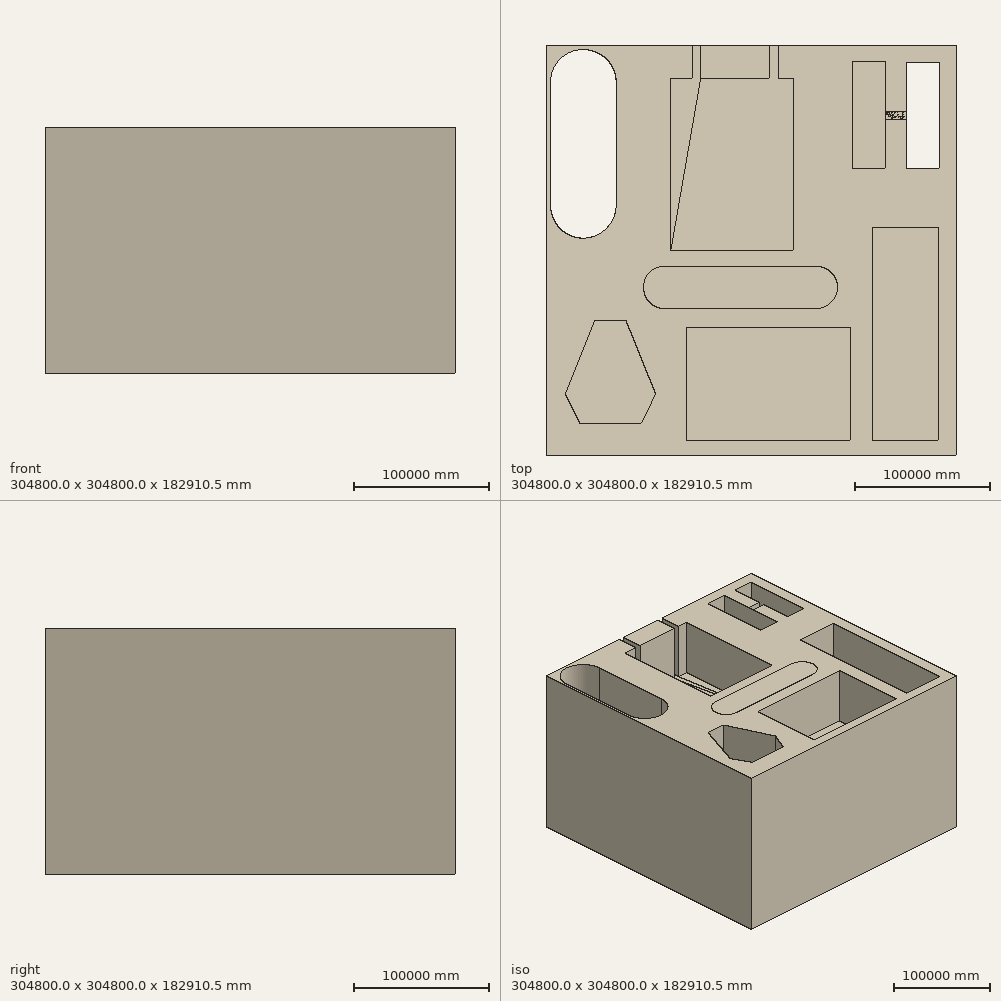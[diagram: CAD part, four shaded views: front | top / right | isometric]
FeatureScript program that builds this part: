
annotation { "Feature Type Name" : "Feature", "Feature Type Description" : "" }
export const myFeature = defineFeature(function(context is Context, id is Id, definition is map)
    precondition{}
    {
        {
            var Q0;
            Q0=qCreatedBy(makeId("Top.planeOp"),FACE);
            var sketch = newSketch(context, id + "F0", { "sketchPlane" : qUnion([Q0])});
            skLineSegment(sketch, "E0.bottom", {"start": v(152400, 152400) * mm, "end": v(-152400, 152400) * mm});
            skLineSegment(sketch, "E0.top", {"start": v(152400, -152400) * mm, "end": v(-152400, -152400) * mm});
            skLineSegment(sketch, "E0.left", {"start": v(152400, 152400) * mm, "end": v(152400, -152400) * mm});
            skLineSegment(sketch, "E0.right", {"start": v(-152400, 152400) * mm, "end": v(-152400, -152400) * mm});
            skPoint(sketch, "E0.middle", {"position": v(0, 0) * mm});
            skLineSegment(sketch, "E1", {"start": v(-149352, 152400) * mm, "end": v(-149352, 124968) * mm});
            skLineSegment(sketch, "E2", {"start": v(-149352, 124968) * mm, "end": v(-152400, 124968) * mm});
            skLineSegment(sketch, "E3.bottom", {"start": v(-149352, 124968) * mm, "end": v(-100584, 124968) * mm});
            skLineSegment(sketch, "E3.top", {"start": v(-149352, 33528) * mm, "end": v(-100584, 33528) * mm});
            skLineSegment(sketch, "E3.left", {"start": v(-149352, 124968) * mm, "end": v(-149352, 33528) * mm});
            skLineSegment(sketch, "E3.right", {"start": v(-100584, 124968) * mm, "end": v(-100584, 33528) * mm});
            skArc(sketch, "E4", {"start": v(-100584, 124968) * mm, "mid": v(-124968, 149352) * mm, "end": v(-149352, 124968) * mm});
            skArc(sketch, "E5", {"start": v(-100584, 33528) * mm, "mid": v(-124968, 9144) * mm, "end": v(-149352, 33528) * mm});
            skLineSegment(sketch, "E6", {"start": v(-124968, 124968) * mm, "end": v(-124968, 149352) * mm});
            skLineSegment(sketch, "E7.bottom", {"start": v(139614.91, 140126.75) * mm, "end": v(115230.91, 140126.75) * mm});
            skLineSegment(sketch, "E7.top", {"start": v(139614.91, 60878.75) * mm, "end": v(115230.91, 60878.75) * mm});
            skLineSegment(sketch, "E7.left", {"start": v(139614.91, 140126.75) * mm, "end": v(139614.91, 60878.75) * mm});
            skLineSegment(sketch, "E7.right", {"start": v(115230.91, 140126.75) * mm, "end": v(115230.91, 60878.75) * mm});
            skSolve(sketch);
        }
        {
            var Q0;
            {var subQ7=sQuery(id+"F0.wireOp",EDGE,"E0.top");Q0=makeQuery(id+"F0.imprint","IMPRINT",FACE,{"disambiguationData":[TD([[makeQuery(id+"F0.imprint","IMPRINT",EDGE,{"derivedFrom":subQ7}),-1.0]])]});}
            var sketch = newSketch(context, id + "F1", { "sketchPlane" : qUnion([Q0])});
            skLineSegment(sketch, "E8.bottom", {"start": v(115322.87, 103222.92) * mm, "end": v(99778.07, 103222.92) * mm});
            skLineSegment(sketch, "E8.top", {"start": v(115322.87, 97126.92) * mm, "end": v(99778.07, 97126.92) * mm});
            skLineSegment(sketch, "E8.left", {"start": v(115322.87, 103222.92) * mm, "end": v(115322.87, 97126.92) * mm});
            skLineSegment(sketch, "E8.right", {"start": v(99778.07, 103222.92) * mm, "end": v(99778.07, 97126.92) * mm});
            skSolve(sketch);
        }
        {
            var Q0;
            {var subQ7=sQuery(id+"F0.wireOp",EDGE,"E0.top");Q0=makeQuery(id+"F0.imprint","IMPRINT",FACE,{"disambiguationData":[TD([[makeQuery(id+"F0.imprint","IMPRINT",EDGE,{"derivedFrom":subQ7}),-1.0]])]});}
            var sketch = newSketch(context, id + "F2", { "sketchPlane" : qUnion([Q0])});
            skLineSegment(sketch, "E9.bottom", {"start": v(99736.5, 140255.87) * mm, "end": v(75352.5, 140255.87) * mm});
            skLineSegment(sketch, "E9.top", {"start": v(99736.5, 61007.87) * mm, "end": v(75352.5, 61007.87) * mm});
            skLineSegment(sketch, "E9.left", {"start": v(99736.5, 140255.87) * mm, "end": v(99736.5, 61007.87) * mm});
            skLineSegment(sketch, "E9.right", {"start": v(75352.5, 140255.87) * mm, "end": v(75352.5, 61007.87) * mm});
            skLineSegment(sketch, "E10.bottom", {"start": v(99736.5, 90581.08) * mm, "end": v(99736.5, 90581.08) * mm});
            skLineSegment(sketch, "E10.top", {"start": v(99736.5, 100631.87) * mm, "end": v(99736.5, 100631.87) * mm});
            skLineSegment(sketch, "E10.left", {"start": v(99736.5, 90581.08) * mm, "end": v(99736.5, 100631.87) * mm});
            skLineSegment(sketch, "E10.right", {"start": v(99736.5, 90581.08) * mm, "end": v(99736.5, 100631.87) * mm});
            skSolve(sketch);
        }
        {
            var Q0;
            {var subQ7=sQuery(id+"F0.wireOp",EDGE,"E0.top");Q0=makeQuery(id+"F0.imprint","IMPRINT",FACE,{"disambiguationData":[TD([[makeQuery(id+"F0.imprint","IMPRINT",EDGE,{"derivedFrom":subQ7}),-1.0]])]});}
            var sketch = newSketch(context, id + "F3", { "sketchPlane" : qUnion([Q0])});
            skLineSegment(sketch, "E11.bottom", {"start": v(139080.24, 17215.46) * mm, "end": v(90312.24, 17215.46) * mm});
            skLineSegment(sketch, "E11.top", {"start": v(139080.24, -141280.54) * mm, "end": v(90312.24, -141280.54) * mm});
            skLineSegment(sketch, "E11.left", {"start": v(139080.24, 17215.46) * mm, "end": v(139080.24, -141280.54) * mm});
            skLineSegment(sketch, "E11.right", {"start": v(90312.24, 17215.46) * mm, "end": v(90312.24, -141280.54) * mm});
            skSolve(sketch);
        }
        {
            var Q0;
            {var subQ7=sQuery(id+"F0.wireOp",EDGE,"E0.top");Q0=makeQuery(id+"F0.imprint","IMPRINT",FACE,{"disambiguationData":[TD([[makeQuery(id+"F0.imprint","IMPRINT",EDGE,{"derivedFrom":subQ7}),-1.0]])]});}
            var sketch = newSketch(context, id + "F4", { "sketchPlane" : qUnion([Q0])});
            skLineSegment(sketch, "E12.bottom", {"start": v(-59924.14, 128016) * mm, "end": v(31515.86, 128016) * mm});
            skLineSegment(sketch, "E12.top", {"start": v(-59924.14, 0) * mm, "end": v(31515.86, 0) * mm});
            skLineSegment(sketch, "E12.left", {"start": v(-59924.14, 128016) * mm, "end": v(-59924.14, 0) * mm});
            skLineSegment(sketch, "E12.right", {"start": v(31515.86, 128016) * mm, "end": v(31515.86, 0) * mm});
            skLineSegment(sketch, "E13.bottom", {"start": v(-43811.4, 152400) * mm, "end": v(-37715.4, 152400) * mm});
            skLineSegment(sketch, "E13.top", {"start": v(-43811.4, 128016) * mm, "end": v(-37715.4, 128016) * mm});
            skLineSegment(sketch, "E13.left", {"start": v(-43811.4, 152400) * mm, "end": v(-43811.4, 128016) * mm});
            skLineSegment(sketch, "E13.right", {"start": v(-37715.4, 152400) * mm, "end": v(-37715.4, 128016) * mm});
            skLineSegment(sketch, "E14.bottom", {"start": v(13740.62, 152400) * mm, "end": v(19836.62, 152400) * mm});
            skLineSegment(sketch, "E14.top", {"start": v(13740.62, 128016) * mm, "end": v(19836.62, 128016) * mm});
            skLineSegment(sketch, "E14.left", {"start": v(13740.62, 152400) * mm, "end": v(13740.62, 128016) * mm});
            skLineSegment(sketch, "E14.right", {"start": v(19836.62, 152400) * mm, "end": v(19836.62, 128016) * mm});
            skSolve(sketch);
        }
        {
            var Q0;
            {var subQ6=sQuery(id+"F1.wireOp",EDGE,"E8.right");Q0=makeQuery(id+"F1.imprint","IMPRINT",FACE,{"disambiguationData":[TD([[makeQuery(id+"F1.imprint","IMPRINT",EDGE,{"derivedFrom":subQ6}),-1.0]])]});}
            var sketch = newSketch(context, id + "F5", { "sketchPlane" : qUnion([Q0])});
            skLineSegment(sketch, "E15.bottom", {"start": v(-48321, -57586.39) * mm, "end": v(73599, -57586.39) * mm});
            skLineSegment(sketch, "E15.top", {"start": v(-48321, -141406.39) * mm, "end": v(73599, -141406.39) * mm});
            skLineSegment(sketch, "E15.left", {"start": v(-48321, -57586.39) * mm, "end": v(-48321, -141406.39) * mm});
            skLineSegment(sketch, "E15.right", {"start": v(73599, -57586.39) * mm, "end": v(73599, -141406.39) * mm});
            skSolve(sketch);
        }
        {
            var Q0;
            {var subQ6=sQuery(id+"F1.wireOp",EDGE,"E8.right");Q0=makeQuery(id+"F1.imprint","IMPRINT",FACE,{"disambiguationData":[TD([[makeQuery(id+"F1.imprint","IMPRINT",EDGE,{"derivedFrom":subQ6}),-1.0]])]});}
            var sketch = newSketch(context, id + "F6", { "sketchPlane" : qUnion([Q0])});
            skLineSegment(sketch, "E16", {"start": v(-127551.5, -128784.93) * mm, "end": v(-81831.5, -128784.93) * mm});
            skLineSegment(sketch, "E17", {"start": v(-81831.5, -128784.93) * mm, "end": v(-71159.45, -106860.36) * mm});
            skLineSegment(sketch, "E18", {"start": v(-71159.45, -106860.36) * mm, "end": v(-93440.34, -51758.63) * mm});
            skLineSegment(sketch, "E19", {"start": v(-93440.34, -51758.63) * mm, "end": v(-116300.34, -51758.63) * mm});
            skLineSegment(sketch, "E20", {"start": v(-116300.34, -51758.63) * mm, "end": v(-138384.57, -106939.47) * mm});
            skLineSegment(sketch, "E21", {"start": v(-138384.57, -106939.47) * mm, "end": v(-127551.5, -128784.93) * mm});
            skSolve(sketch);
        }
        {
            var Q0;
            Q0 = qSketchRegion(id + "F1", true);
            var Q1;
            Q1 = qSketchRegion(id + "F6", true);
            var Q2;
            Q2 = qSketchRegion(id + "F4", true);
            var Q3;
            Q3 = qSketchRegion(id + "F0", true);
            var Q4;
            Q4 = qSketchRegion(id + "F5", true);
            var Q5;
            Q5 = qSketchRegion(id + "F2", true);
            var Q6;
            Q6 = qSketchRegion(id + "F3", true);
            extrude(context, id + "F7", {"entities" : qUnion([Q0, Q1, Q2, Q3, Q4, Q5, Q6]), "depth" : 182880 * mm, "offsetDistance" : 30.48 * mm});
        }
        {
            var Q0;
            Q0=makeQuery(id+"F7.opExtrude","CAP_FACE",FACE,{"disambiguationData":[OSD([sQuery(id+"F4.wireOp",EDGE,"E12.bottom"),sQuery(id+"F4.wireOp",EDGE,"E12.top"),sQuery(id+"F4.wireOp",EDGE,"E12.left"),sQuery(id+"F4.wireOp",EDGE,"E12.right"),sQuery(id+"F4.wireOp",EDGE,"E13.bottom"),sQuery(id+"F4.wireOp",EDGE,"E13.left"),sQuery(id+"F4.wireOp",EDGE,"E13.right"),sQuery(id+"F4.wireOp",EDGE,"E14.bottom"),sQuery(id+"F4.wireOp",EDGE,"E14.left"),sQuery(id+"F4.wireOp",EDGE,"E14.right")])],"isStart":false});
            extrude(context, id + "F8", {"entities" : qUnion([Q0]), "operationType" : NewBodyOperationType.REMOVE, "oppositeDirection" : true, "depth" : 60960 * mm, "offsetDistance" : 30.48 * mm});
        }
        {
            var Q0;
            Q0=makeQuery(id+"F7.opExtrude","CAP_FACE",FACE,{"disambiguationData":[OSD([sQuery(id+"F1.wireOp",EDGE,"E8.bottom"),sQuery(id+"F1.wireOp",EDGE,"E8.top"),sQuery(id+"F1.wireOp",EDGE,"E8.left"),sQuery(id+"F1.wireOp",EDGE,"E8.right")])],"isStart":false});
            var Q1;
            Q1=makeQuery(id+"F7.opExtrude","CAP_FACE",FACE,{"disambiguationData":[OSD([sQuery(id+"F6.wireOp",EDGE,"E16"),sQuery(id+"F6.wireOp",EDGE,"E17"),sQuery(id+"F6.wireOp",EDGE,"E18"),sQuery(id+"F6.wireOp",EDGE,"E19"),sQuery(id+"F6.wireOp",EDGE,"E20"),sQuery(id+"F6.wireOp",EDGE,"E21")])],"isStart":false});
            var Q2;
            Q2=makeQuery(id+"F7.opExtrude","CAP_FACE",FACE,{"disambiguationData":[OSD([sQuery(id+"F2.wireOp",EDGE,"E9.bottom"),sQuery(id+"F2.wireOp",EDGE,"E9.top"),sQuery(id+"F2.wireOp",EDGE,"E9.left"),sQuery(id+"F2.wireOp",EDGE,"E9.right"),sQuery(id+"F2.wireOp",EDGE,"E10.right")])],"isStart":false});
            var Q3;
            Q3=makeQuery(id+"F7.opExtrude","CAP_FACE",FACE,{"disambiguationData":[OSD([sQuery(id+"F3.wireOp",EDGE,"E11.bottom"),sQuery(id+"F3.wireOp",EDGE,"E11.top"),sQuery(id+"F3.wireOp",EDGE,"E11.left"),sQuery(id+"F3.wireOp",EDGE,"E11.right")])],"isStart":false});
            var Q4;
            Q4=makeQuery(id+"F7.opExtrude","CAP_FACE",FACE,{"disambiguationData":[OSD([sQuery(id+"F5.wireOp",EDGE,"E15.bottom"),sQuery(id+"F5.wireOp",EDGE,"E15.top"),sQuery(id+"F5.wireOp",EDGE,"E15.left"),sQuery(id+"F5.wireOp",EDGE,"E15.right")])],"isStart":false});
            extrude(context, id + "F9", {"entities" : qUnion([Q0, Q1, Q2, Q3, Q4]), "operationType" : NewBodyOperationType.REMOVE, "oppositeDirection" : true, "depth" : 60960 * mm, "offsetDistance" : 30.48 * mm});
        }
        {
            var Q0;
            {var subQ0=sQuery(id+"F0.wireOp",EDGE,"E7.bottom");var subQ1=sQuery(id+"F0.wireOp",EDGE,"E5");var subQ5=sQuery(id+"F0.wireOp",EDGE,"E4");var subQ6=sQuery(id+"F0.wireOp",EDGE,"E3.right");var subQ7=sQuery(id+"F0.wireOp",EDGE,"E3.left");var subQ8=sQuery(id+"F0.wireOp",EDGE,"E7.top");var subQ11=sQuery(id+"F0.wireOp",EDGE,"E0.bottom");var subQ12=sQuery(id+"F0.wireOp",EDGE,"E0.right");var subQ13=sQuery(id+"F0.wireOp",EDGE,"E0.top");var subQ14=sQuery(id+"F0.wireOp",EDGE,"E0.left");var subQ15=sQuery(id+"F0.wireOp",EDGE,"E7.left");var subQ16=sQuery(id+"F0.wireOp",EDGE,"E7.right");Q0=makeQuery(id+"F8.boolean.opBoolean","SPLIT",FACE,{"disambiguationData":[TD([makeQuery(id+"F7.opExtrude","SWEPT_FACE",FACE,{"disambiguationData":[OSD([subQ13])]})])],"derivedFrom":makeQuery(id+"F7.opExtrude","CAP_FACE",FACE,{"disambiguationData":[OSD([subQ11,subQ13,subQ14,subQ12,subQ7,subQ6,subQ5,subQ1,subQ0,subQ8,subQ15,subQ16])],"isStart":false})});}
            var sketch = newSketch(context, id + "F10", { "sketchPlane" : qUnion([Q0])});
            skLineSegment(sketch, "E22", {"start": v(-66410.8, -11879.89) * mm, "end": v(46365.2, -11879.89) * mm});
            skSolve(sketch);
        }
        {
            var Q0;
            {var subQ14=sQuery(id+"F0.wireOp",EDGE,"E0.top");Q0=makeQuery(id+"F10.imprint","IMPRINT",FACE,{"disambiguationData":[TD([[makeQuery(id+"F10.imprint","IMPRINT",EDGE,{"derivedFrom":makeQuery(id+"F7.opExtrude","CAP_EDGE",EDGE,{"disambiguationData":[OSD([subQ14])],"isStart":false})}),-1.0]])]});}
            var sketch = newSketch(context, id + "F11", { "sketchPlane" : qUnion([Q0])});
            skLineSegment(sketch, "E23", {"start": v(-64535.09, -43243.24) * mm, "end": v(48240.91, -43243.24) * mm});
            skSolve(sketch);
        }
        {
            var Q0;
            {var subQ14=sQuery(id+"F0.wireOp",EDGE,"E0.top");Q0=makeQuery(id+"F11.imprint","IMPRINT",FACE,{"disambiguationData":[TD([[makeQuery(id+"F11.imprint","IMPRINT",EDGE,{"derivedFrom":makeQuery(id+"F10.imprint","IMPRINT",EDGE,{"derivedFrom":makeQuery(id+"F7.opExtrude","CAP_EDGE",EDGE,{"disambiguationData":[OSD([subQ14])],"isStart":false})})}),-1.0]])]});}
            var sketch = newSketch(context, id + "F12", { "sketchPlane" : qUnion([Q0])});
            skArc(sketch, "E24", {"start": v(48163.47, -43076.49) * mm, "mid": v(63377.53, -26706.15) * mm, "end": v(46560.92, -11986.89) * mm});
            skSolve(sketch);
        }
        {
            var Q0;
            {var subQ14=sQuery(id+"F0.wireOp",EDGE,"E0.top");Q0=makeQuery(id+"F11.imprint","IMPRINT",FACE,{"disambiguationData":[TD([[makeQuery(id+"F11.imprint","IMPRINT",EDGE,{"derivedFrom":makeQuery(id+"F10.imprint","IMPRINT",EDGE,{"derivedFrom":makeQuery(id+"F7.opExtrude","CAP_EDGE",EDGE,{"disambiguationData":[OSD([subQ14])],"isStart":false})})}),-1.0]])]});}
            var sketch = newSketch(context, id + "F13", { "sketchPlane" : qUnion([Q0])});
            skArc(sketch, "E25", {"start": v(-66126.57, -12153.64) * mm, "mid": v(-80611.47, -28550.92) * mm, "end": v(-64445.05, -43293.04) * mm});
            skSolve(sketch);
        }
        {
            var Q0;
            {var subQ14=sQuery(id+"F0.wireOp",EDGE,"E0.top");Q0=makeQuery(id+"F10.imprint","IMPRINT",FACE,{"disambiguationData":[TD([[makeQuery(id+"F10.imprint","IMPRINT",EDGE,{"derivedFrom":makeQuery(id+"F7.opExtrude","CAP_EDGE",EDGE,{"disambiguationData":[OSD([subQ14])],"isStart":false})}),-1.0]])]});}
            var sketch = newSketch(context, id + "F14", { "sketchPlane" : qUnion([Q0])});
            skLineSegment(sketch, "E26.0", {"start": v(-66410.8, -11879.89) * mm, "end": v(46365.2, -11879.89) * mm});
            skArc(sketch, "E27.0", {"start": v(-66126.57, -12153.64) * mm, "mid": v(-80611.47, -28550.92) * mm, "end": v(-64445.05, -43293.04) * mm});
            skLineSegment(sketch, "E28.0", {"start": v(-64535.09, -43243.24) * mm, "end": v(48240.91, -43243.24) * mm});
            skArc(sketch, "E29.0", {"start": v(48163.47, -43076.49) * mm, "mid": v(63377.53, -26706.15) * mm, "end": v(46560.92, -11986.89) * mm});
            skSolve(sketch);
        }
        {
            var Q0;
            Q0=sQuery(id+"F14.wireOp",EDGE,"E26.0");
            var Q1;
            Q1=sQuery(id+"F14.wireOp",EDGE,"E29.0");
            var Q2;
            Q2=sQuery(id+"F14.wireOp",EDGE,"E28.0");
            var Q3;
            Q3=sQuery(id+"F14.wireOp",EDGE,"E27.0");
            extrude(context, id + "F15", {"bodyType" : ToolBodyType.SURFACE, "surfaceEntities" : qUnion([Q0, Q1, Q2, Q3]), "oppositeDirection" : true, "depth" : 11887.2 * mm, "offsetDistance" : 30.48 * mm});
        }
        {
            var Q0;
            {var subQ14=sQuery(id+"F0.wireOp",EDGE,"E0.top");Q0=makeQuery(id+"F10.imprint","IMPRINT",FACE,{"disambiguationData":[TD([[makeQuery(id+"F10.imprint","IMPRINT",EDGE,{"derivedFrom":makeQuery(id+"F7.opExtrude","CAP_EDGE",EDGE,{"disambiguationData":[OSD([subQ14])],"isStart":false})}),-1.0]])]});}
            var sketch = newSketch(context, id + "F16", { "sketchPlane" : qUnion([Q0])});
            skLineSegment(sketch, "E30.0", {"start": v(-64535.09, -43243.24) * mm, "end": v(48240.91, -43243.24) * mm});
            skLineSegment(sketch, "E31.0", {"start": v(-66410.8, -11879.89) * mm, "end": v(46365.2, -11879.89) * mm});
            skArc(sketch, "E32", {"start": v(48240.91, -43243.24) * mm, "mid": v(63950.61, -26565.94) * mm, "end": v(46365.2, -11879.89) * mm});
            skArc(sketch, "E33", {"start": v(-64535.09, -43243.24) * mm, "mid": v(-80244.78, -28445) * mm, "end": v(-66410.8, -11879.89) * mm});
            skSolve(sketch);
        }
        {
            var Q0;
            Q0=makeQuery(id+"F16.imprint","IMPRINT",FACE,{"disambiguationData":[TD([[makeQuery(id+"F16.imprint","IMPRINT",EDGE,{"derivedFrom":sQuery(id+"F16.wireOp",EDGE,"E30.0")}),1.0]])]});
            extrude(context, id + "F17", {"entities" : qUnion([Q0]), "operationType" : NewBodyOperationType.ADD, "depth" : 30.48 * mm, "offsetDistance" : 30.48 * mm});
        }
    });
